# Revit family: QF_ELECTROLUXPROFESSIONAL_232225_SM6V150
name_source: partatom
category: Specialty Equipment
revit_build: Autodesk Revit 2018 (Build: 20190510_1515(x64)
units: mm (PartAtom-declared; Revit-internal decimal feet)

## family parameters
Always vertical = Yes
Cut with Voids When Loaded = No
Part Type = Normal
Room Calculation Point = No
Round Connector Dimension = Use Diameter
Shared = No
Work Plane-Based = No

## types (1)
- Standard
    Accessory = Yes
    B_Diameter = 816 mm  [stored 2.67717 ft]
    Base2Depth = 940 mm  [stored 3.08399 ft]
    Base2Width = 245 mm  [stored 0.803806 ft]
    Cold Water Size = 19 mm
    Compressed Air Pressure = 0.0 Pa
    Compressed Air Size = 0 mm
    Compressed Air Volume = 0.0 L/s
    Condensate Return Size = 0 mm
    Cycle = 60 Hz
    D = 250 mm  [stored 0.82021 ft]
    Depth Actual = 1070 mm  [stored 3.5105 ft]
    Description = EL.PAN+STIRRER 150 LT, H=600, VARIOMIX
    Direct Waste Size = 0 mm
    Gas Input Pressure = 0
    Gas KW = 0
    Gas Size = 0 mm
    HP = 42.2 HP
    Height Actual = 1050 mm  [stored 3.44488 ft]
    Hot Water Size = 13 mm
    Item Number = 232225
    K = 600 mm
    K_back = 200 mm  [stored 0.656168 ft]
    L = 900 mm  [stored 2.95276 ft]
    L_Back = 335 mm  [stored 1.09908 ft]
    Length Actual = 1300 mm  [stored 4.26509 ft]
    Manufacturer = Electrolux Professional
    Model = SM6V150
    N = 1480 mm  [stored 4.85564 ft]
    Phase = 3
    R-5 = 880 mm  [stored 2.88714 ft]
    R2 = 442.5 mm
    Refrigerant Compressor Remote = Yes
    Refrigeration Liquid Line Size = 0 mm
    Refrigeration Suction Line Size = 0 mm
    Right = 690 mm  [stored 2.26378 ft]
    Steam Pounds per Hour = 0
    Steam Supply Maximum Pressure = 0.0 Pa
    Steam Supply Minimum Pressure = 0.0 Pa
    Steam Supply Size = 0 mm
    T = 305 mm  [stored 1.00066 ft]
    URL = http://professional.electrolux.com
    URL Manufacturer = http://professional.electrolux.com
    Volts = 400 V
    Watts = 0 W
    Weight = 315.00 kg

note: source unit labels omitted for Gas Input Pressure — the stored unit's dimension contradicts the parameter name (converter mislabeling)

note: [stored X ft] marks values corroborated as IEEE doubles in the binary element streams (Revit-internal decimal feet)

## geometry (parser evidence)
native form markers: Revolve x3, Sweep x11
no freeform markers — native parametric forms only
